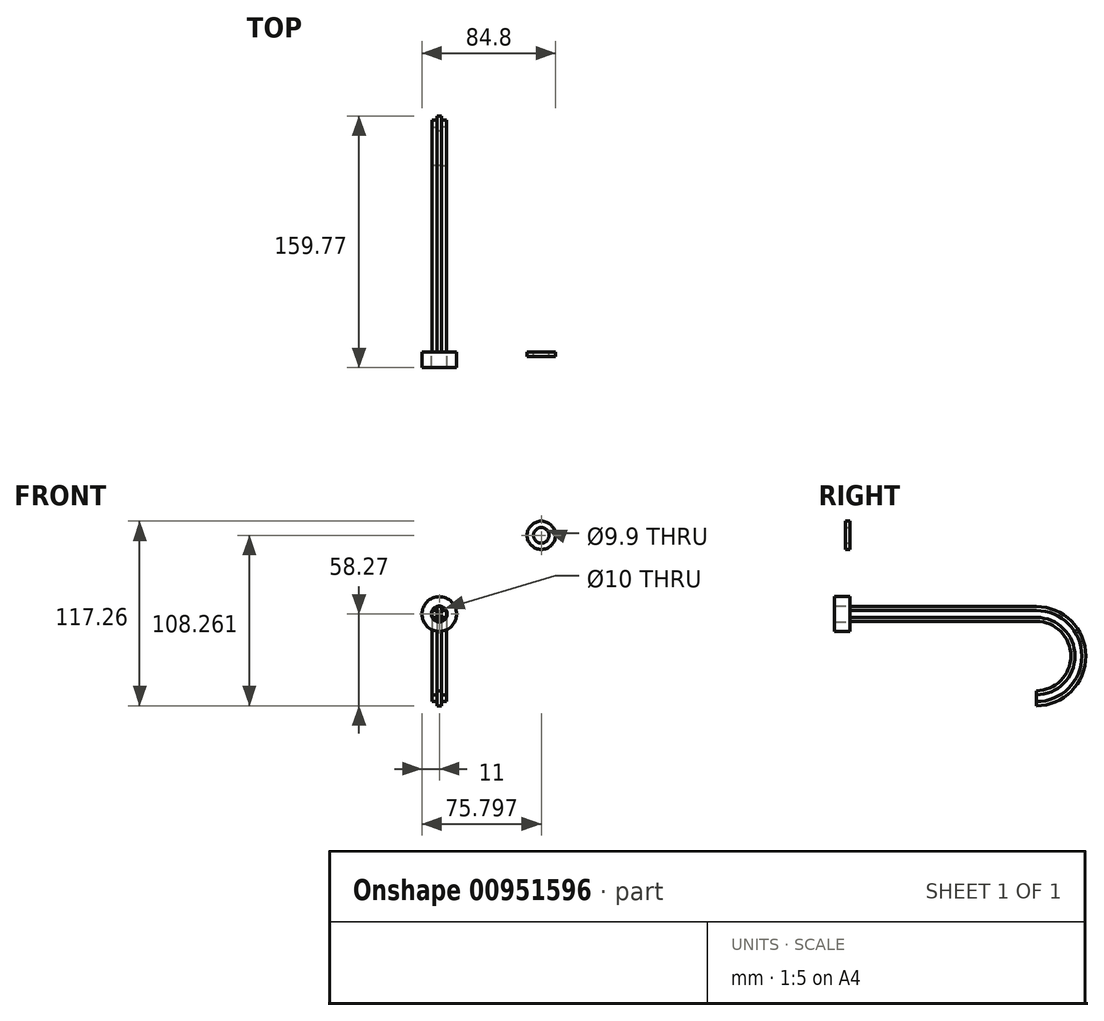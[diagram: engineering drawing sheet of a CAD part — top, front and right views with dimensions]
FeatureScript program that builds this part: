
annotation { "Feature Type Name" : "Feature", "Feature Type Description" : "" }
export const myFeature = defineFeature(function(context is Context, id is Id, definition is map)
    precondition{}
    {
        {
            var Q0;
            Q0=qCreatedBy(makeId("Front.planeOp"),FACE);
            var sketch = newSketch(context, id + "F0", { "sketchPlane" : qUnion([Q0])});
            skCircle(sketch, "E0", {"center": v(0, 0) * mm, "radius": 11 * mm});
            skCircle(sketch, "E1", {"center": v(0, 0) * mm, "radius": 5 * mm});
            skSolve(sketch);
        }
        {
            var Q0;
            Q0=makeQuery(id+"F0.imprint","IMPRINT",FACE,{"disambiguationData":[TD([[makeQuery(id+"F0.imprint","IMPRINT",EDGE,{"derivedFrom":sQuery(id+"F0.wireOp",EDGE,"E0")}),1.0]])]});
            extrude(context, id + "F1", {"entities" : qUnion([Q0]), "depth" : 10 * mm, "offsetDistance" : 25 * mm});
        }
        {
            var Q0;
            Q0=qCreatedBy(makeId("Front.planeOp"),FACE);
            var sketch = newSketch(context, id + "F2", { "sketchPlane" : qUnion([Q0])});
            skCircle(sketch, "E2.0", {"center": v(0, 0) * mm, "radius": 5 * mm, "construction": true});
            skLineSegment(sketch, "E3.bottom", {"start": v(1.5, 4.77) * mm, "end": v(-1.5, 4.77) * mm});
            skLineSegment(sketch, "E3.top", {"start": v(1.5, -4.77) * mm, "end": v(-1.5, -4.77) * mm});
            skLineSegment(sketch, "E3.right", {"start": v(-1.5, 4.77) * mm, "end": v(-1.5, -4.77) * mm});
            skLineSegment(sketch, "E4", {"start": v(-5, 0) * mm, "end": v(5, 0) * mm, "construction": true});
            skPoint(sketch, "E4.endSnap0", {"position": v(1.5, 0) * mm});
            skLineSegment(sketch, "E5", {"start": v(0, 4.77) * mm, "end": v(0, -4.77) * mm, "construction": true});
            skLineSegment(sketch, "E6", {"start": v(1.5, 4.77) * mm, "end": v(1.5, -4.77) * mm});
            skSolve(sketch);
        }
        {
            var Q0;
            Q0=qCreatedBy(makeId("Front.planeOp"),FACE);
            var sketch = newSketch(context, id + "F3", { "sketchPlane" : qUnion([Q0])});
            skCircle(sketch, "E7.0", {"center": v(0, 0) * mm, "radius": 5 * mm, "construction": true});
            skLineSegment(sketch, "E8.0", {"start": v(1.5, 4.77) * mm, "end": v(-1.5, 4.77) * mm, "construction": true});
            skLineSegment(sketch, "E9.0", {"start": v(1.5, 4.77) * mm, "end": v(1.5, -4.77) * mm, "construction": true});
            skLineSegment(sketch, "E10", {"start": v(-5, 0) * mm, "end": v(5, 0) * mm, "construction": true});
            skPoint(sketch, "E11", {"position": v(3, 0) * mm});
            skLineSegment(sketch, "E12.bottom", {"start": v(1.5, 2.18) * mm, "end": v(4.5, 2.18) * mm});
            skLineSegment(sketch, "E12.top", {"start": v(1.5, -2.18) * mm, "end": v(4.5, -2.18) * mm});
            skLineSegment(sketch, "E12.left", {"start": v(1.5, 2.18) * mm, "end": v(1.5, -2.18) * mm});
            skLineSegment(sketch, "E12.right", {"start": v(4.5, 2.18) * mm, "end": v(4.5, -2.18) * mm});
            skSolve(sketch);
        }
        {
            var Q0;
            Q0=qCreatedBy(makeId("Right.planeOp"),FACE);
            var sketch = newSketch(context, id + "F4", { "sketchPlane" : qUnion([Q0])});
            skLineSegment(sketch, "E13", {"start": v(0, 0) * mm, "end": v(118.25, 0) * mm});
            skLineSegment(sketch, "E14", {"start": v(118.25, 0) * mm, "end": v(118.25, -53.5) * mm, "construction": true});
            skArc(sketch, "E15", {"start": v(118.25, -53.5) * mm, "mid": v(145, -26.75) * mm, "end": v(118.25, 0) * mm});
            skSolve(sketch);
        }
        {
            var Q0;
            Q0 = qSketchRegion(id + "F2", true);
            var Q1;
            Q1 = qConstructionFilter(qBodyType(qCreatedBy(id + "F4" ,EDGE), BodyType.WIRE), ConstructionObject.NO);
            sweep(context, id + "F5", {"profiles" : qUnion([Q0]), "path" : qUnion([Q1])});
        }
        {
            var Q0;
            Q0 = qSketchRegion(id + "F3", true);
            var Q1;
            Q1 = qConstructionFilter(qBodyType(qCreatedBy(id + "F3" ,EDGE), BodyType.WIRE), ConstructionObject.NO);
            var Q2;
            Q2 = qConstructionFilter(qBodyType(qCreatedBy(id + "F4" ,EDGE), BodyType.WIRE), ConstructionObject.NO);
            sweep(context, id + "F6", {"profiles" : qUnion([Q0]), "surfaceProfiles" : qUnion([Q1]), "path" : qUnion([Q2])});
        }
        {
            var Q0;
            Q0=makeQuery(id+"F6.opSweep","SWEPT_BODY",BODY,{"disambiguationData":[OSD([sQuery(id+"F3.wireOp",EDGE,"E12.bottom"),sQuery(id+"F3.wireOp",EDGE,"E12.top"),sQuery(id+"F3.wireOp",EDGE,"E12.left"),sQuery(id+"F3.wireOp",EDGE,"E12.right"),sQuery(id+"F4.wireOp",EDGE,"E15")])]});
            var Q1;
            Q1=qCreatedBy(makeId("Right.planeOp"),FACE);
            mirror(context, id + "F7", {"entities" : qUnion([Q0]), "mirrorPlane" : qUnion([Q1])});
        }
        {
            var Q0;
            Q0=qCreatedBy(makeId("Front.planeOp"),FACE);
            var sketch = newSketch(context, id + "F8", { "sketchPlane" : qUnion([Q0])});
            skCircle(sketch, "E16", {"center": v(64.8, 50) * mm, "radius": 4.95 * mm});
            skCircle(sketch, "E17", {"center": v(64.8, 50) * mm, "radius": 9 * mm});
            skSolve(sketch);
        }
        {
            var Q0;
            Q0=makeQuery(id+"F8.imprint","IMPRINT",FACE,{"disambiguationData":[TD([[makeQuery(id+"F8.imprint","IMPRINT",EDGE,{"derivedFrom":sQuery(id+"F8.wireOp",EDGE,"E16")}),-1.0]])]});
            extrude(context, id + "F9", {"entities" : qUnion([Q0]), "depth" : 3 * mm, "offsetDistance" : 25 * mm});
        }
    });
